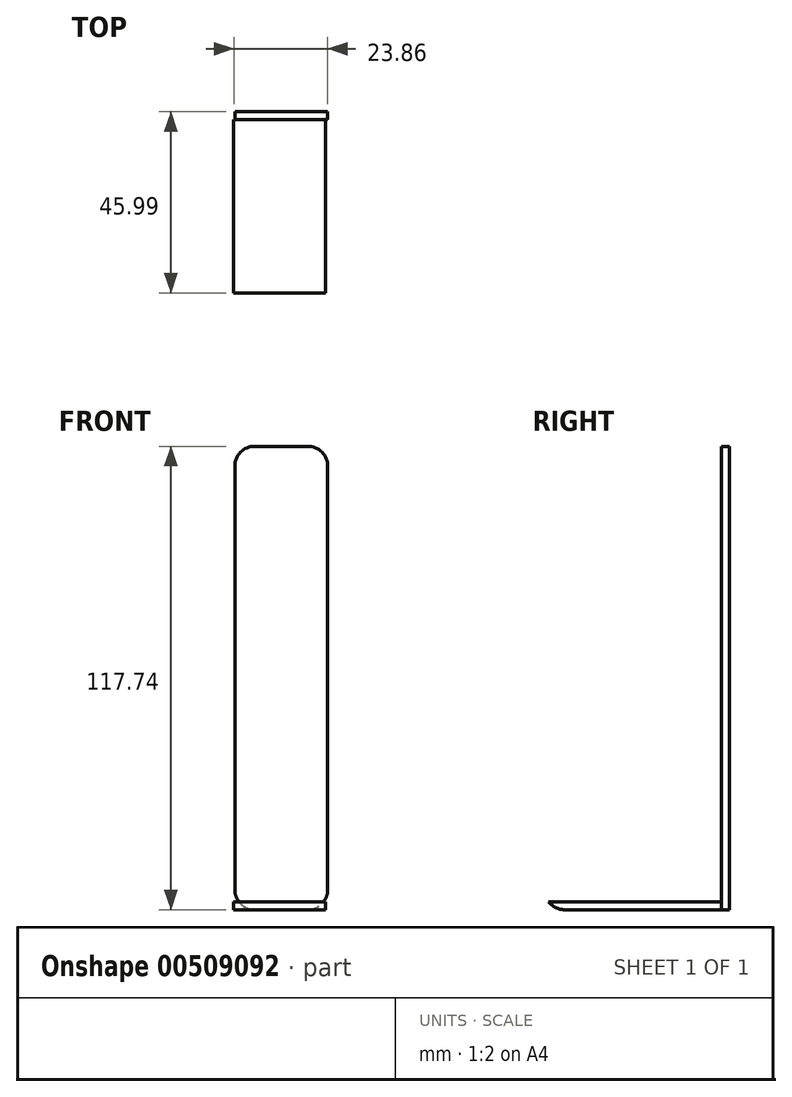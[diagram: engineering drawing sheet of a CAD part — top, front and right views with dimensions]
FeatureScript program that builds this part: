
annotation { "Feature Type Name" : "Feature", "Feature Type Description" : "" }
export const myFeature = defineFeature(function(context is Context, id is Id, definition is map)
    precondition{}
    {
        {
            var Q0;
            Q0=qCreatedBy(makeId("Front.planeOp"),FACE);
            var sketch = newSketch(context, id + "F0", { "sketchPlane" : qUnion([Q0])});
            skLineSegment(sketch, "E0.bottom", {"start": v(-13.75, 47.07) * mm, "end": v(9.86, 47.07) * mm});
            skLineSegment(sketch, "E0.top", {"start": v(-13.75, -70.67) * mm, "end": v(9.86, -70.67) * mm});
            skLineSegment(sketch, "E0.left", {"start": v(-13.75, 47.07) * mm, "end": v(-13.75, -70.67) * mm});
            skLineSegment(sketch, "E0.right", {"start": v(9.86, 47.07) * mm, "end": v(9.86, -70.67) * mm});
            skSolve(sketch);
        }
        {
            var Q0;
            Q0 = qSketchRegion(id + "F0", true);
            extrude(context, id + "F1", {"entities" : qUnion([Q0]), "oppositeDirection" : true, "depth" : 2.03 * mm, "offsetDistance" : 25.4 * mm});
        }
        {
            var Q0;
            Q0=makeQuery(id+"F1.opExtrude","SWEPT_EDGE",EDGE,{"disambiguationData":[OSD([sQuery(id+"F0.wireOp",EDGE,"E0.bottom"),sQuery(id+"F0.wireOp",EDGE,"E0.left")])]});
            var Q1;
            Q1=makeQuery(id+"F1.opExtrude","SWEPT_EDGE",EDGE,{"disambiguationData":[OSD([sQuery(id+"F0.wireOp",EDGE,"E0.bottom"),sQuery(id+"F0.wireOp",EDGE,"E0.right")])]});
            var Q2;
            Q2=makeQuery(id+"F1.opExtrude","SWEPT_EDGE",EDGE,{"disambiguationData":[OSD([sQuery(id+"F0.wireOp",EDGE,"E0.top"),sQuery(id+"F0.wireOp",EDGE,"E0.right")])]});
            var Q3;
            Q3=makeQuery(id+"F1.opExtrude","SWEPT_EDGE",EDGE,{"disambiguationData":[OSD([sQuery(id+"F0.wireOp",EDGE,"E0.top"),sQuery(id+"F0.wireOp",EDGE,"E0.left")])]});
            fillet(context, id + "F2", {"entities" : qUnion([Q0, Q1, Q2, Q3]), "radius" : 5.08 * mm, "tangentPropagation" : true, "allowEdgeOverflow" : false});
        }
        {
            var Q0;
            Q0=makeQuery(id+"F1.opExtrude","SWEPT_FACE",FACE,{"disambiguationData":[OSD([sQuery(id+"F0.wireOp",EDGE,"E0.top")])]});
            var sketch = newSketch(context, id + "F3", { "sketchPlane" : qUnion([Q0])});
            skLineSegment(sketch, "E1.bottom", {"start": v(-14, 0) * mm, "end": v(9.34, 0) * mm});
            skLineSegment(sketch, "E1.top", {"start": v(-14, 43.96) * mm, "end": v(9.34, 43.96) * mm});
            skLineSegment(sketch, "E1.left", {"start": v(-14, 0) * mm, "end": v(-14, 43.96) * mm});
            skLineSegment(sketch, "E1.right", {"start": v(9.34, 0) * mm, "end": v(9.34, 43.96) * mm});
            skSolve(sketch);
        }
        {
            var Q0;
            Q0 = qSketchRegion(id + "F3", true);
            extrude(context, id + "F4", {"entities" : qUnion([Q0]), "operationType" : NewBodyOperationType.ADD, "oppositeDirection" : true, "depth" : 2.03 * mm, "offsetDistance" : 25.4 * mm});
        }
        {
            var Q0;
            Q0=makeQuery(id+"F4.opExtrude","CAP_EDGE",EDGE,{"disambiguationData":[OSD([sQuery(id+"F3.wireOp",EDGE,"E1.top")])],"isStart":true});
            fillet(context, id + "F5", {"entities" : qUnion([Q0]), "radius" : 5.08 * mm, "tangentPropagation" : true, "allowEdgeOverflow" : false});
        }
    });
